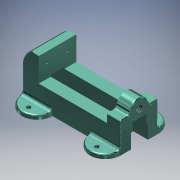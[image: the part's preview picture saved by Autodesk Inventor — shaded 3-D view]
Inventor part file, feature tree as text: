
AUTODESK INVENTOR PART (.ipt)
format: ipt  version: 2017 (Build 210142000, 142)  size: 377,344 bytes
history: native  units: in
note: dims shown in document units (in); Inventor stores cm internally (conversion verified against a paired STEP export)
features: extrude x4, sketch x4, hole x3, plane x2, mirror x2, fillet x2
ambient origin geometry x8: Origin, YZ Plane, XZ Plane, XY Plane, X Axis, Y Axis, Z Axis, Center Point
bodies: Solid1 (feature_tree)
feature tree (17):
  extrude  "Extrusion1"  Depth=7.25in
  extrude  "Extrusion2"  Depth=0.625in
  plane  "Work Plane2"
  mirror  "Mirror1"
  plane  "Work Plane3"
  mirror  "Mirror3"
  extrude  "Extrusion3"  Depth=1.1875in
  extrude  "Extrusion4"  Depth=0.625in
  fillet  "1/4R Fillet"  Radius=2.75in
  fillet  "1/8R Fillet"  Radius=1.125in
  hole  "5/8-8ACME"  [1 undecoded]
  hole  "(1) 1/4-20UNC-2B"  [1 undecoded]
  hole  "(2) 1/4-20UNC-2B"  [1 undecoded]
  sketch  "Sketch1"  dims[d0=7.25in d1=2.1875in]
  sketch  "Sketch2"  dims[d4=1.0in d5=0.625in]
  sketch  "Sketch3"  dims[d6=5.0in d7=1.1875in]
  sketch  "Sketch4"  dims[d8=1.375in d9=3.3125in d10=2.75in d11=0.0in d12=1.125in d14=0.3125in d16=2.25in d17=0.625in d18=1.125in d23=0.3125in d24=0.0in d26=-1.375in d27=-3.625in d28=2.25in d29=1.375in d30=1.375in d31=1.0in d32=0.0in d33=1.375in d34=0.501in d35=0.626in d36=1.002in d37=1.252in d38=1.0625in d39=1.6875in d40=3.5in d41=1.0in d42=0.0in d43=0.25in d44=0.125in d63=1.0in d64=1.0in d47=0.5in d48=1.0in d49=0.119in d50=0.25in d51=0.5635in d52=0.146in d53=0.0in d54=1.0in d55=0.625in d56=0.196in d57=0.5in d58=0.119in d59=0.25in d60=0.5635in d61=0.625in d62=0.0in d65=2.125in d66=1.0in d67=0.196in d68=0.625in d69=0.119in d70=0.25in d71=0.5635in d72=0.625in d73=0.0in]
note: 3 required parameter values undecoded (feature->parameter linkage not recoverable at this tier; creation-order binding heuristic only, values carry confidence <= 0.55)
